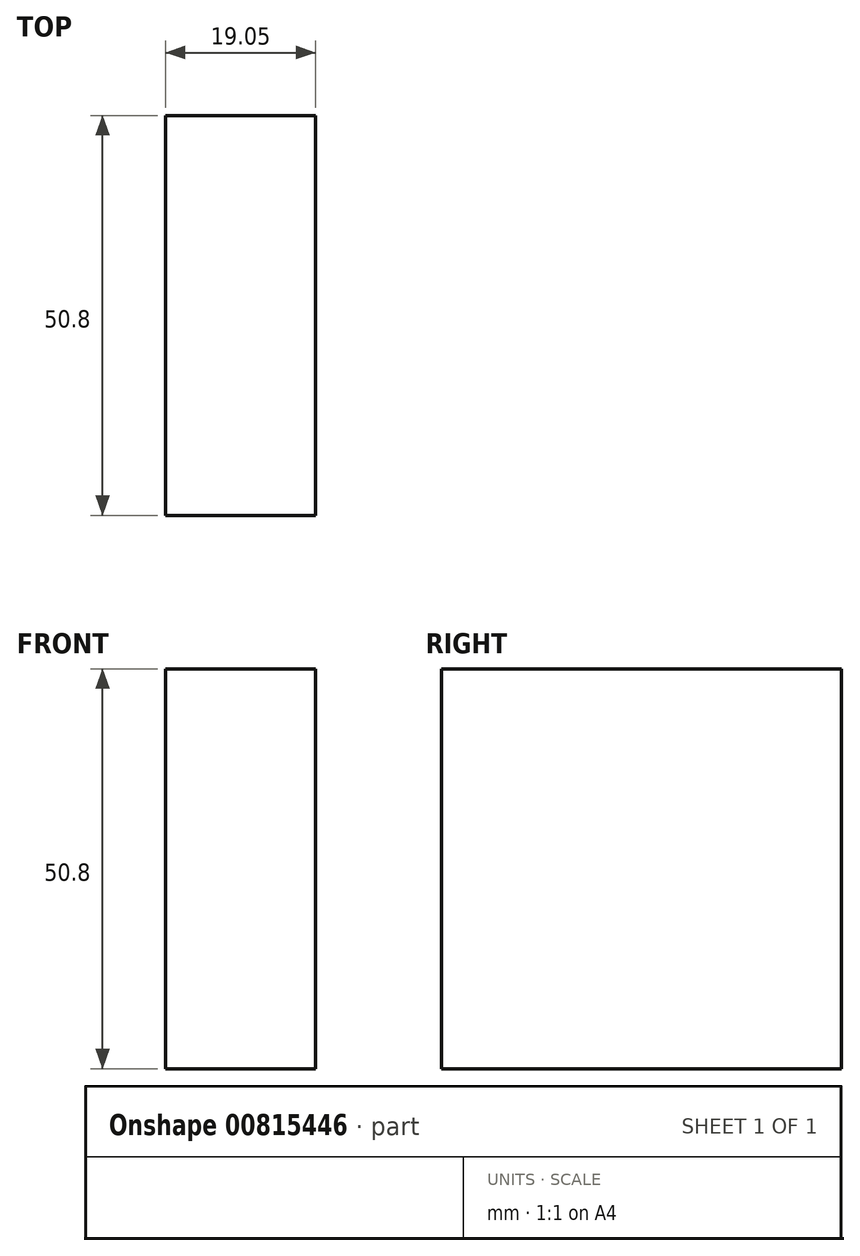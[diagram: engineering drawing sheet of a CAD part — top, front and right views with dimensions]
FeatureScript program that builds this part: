
annotation { "Feature Type Name" : "Feature", "Feature Type Description" : "" }
export const myFeature = defineFeature(function(context is Context, id is Id, definition is map)
    precondition{}
    {
        {
            var Q0;
            Q0=qCreatedBy(makeId("Front.planeOp"),FACE);
            var sketch = newSketch(context, id + "F0", { "sketchPlane" : qUnion([Q0])});
            skLineSegment(sketch, "E0", {"start": v(0, 0) * mm, "end": v(0, 50.8) * mm});
            skLineSegment(sketch, "E1", {"start": v(0, 50.8) * mm, "end": v(19.05, 50.8) * mm});
            skLineSegment(sketch, "E2", {"start": v(19.05, 50.8) * mm, "end": v(19.05, 0) * mm});
            skLineSegment(sketch, "E3", {"start": v(19.05, 0) * mm, "end": v(0, 0) * mm});
            skSolve(sketch);
        }
        {
            var Q0;
            Q0 = qSketchRegion(id + "F0", true);
            extrude(context, id + "F1", {"entities" : qUnion([Q0]), "depth" : 50.8 * mm, "offsetDistance" : 25.4 * mm});
        }
    });
